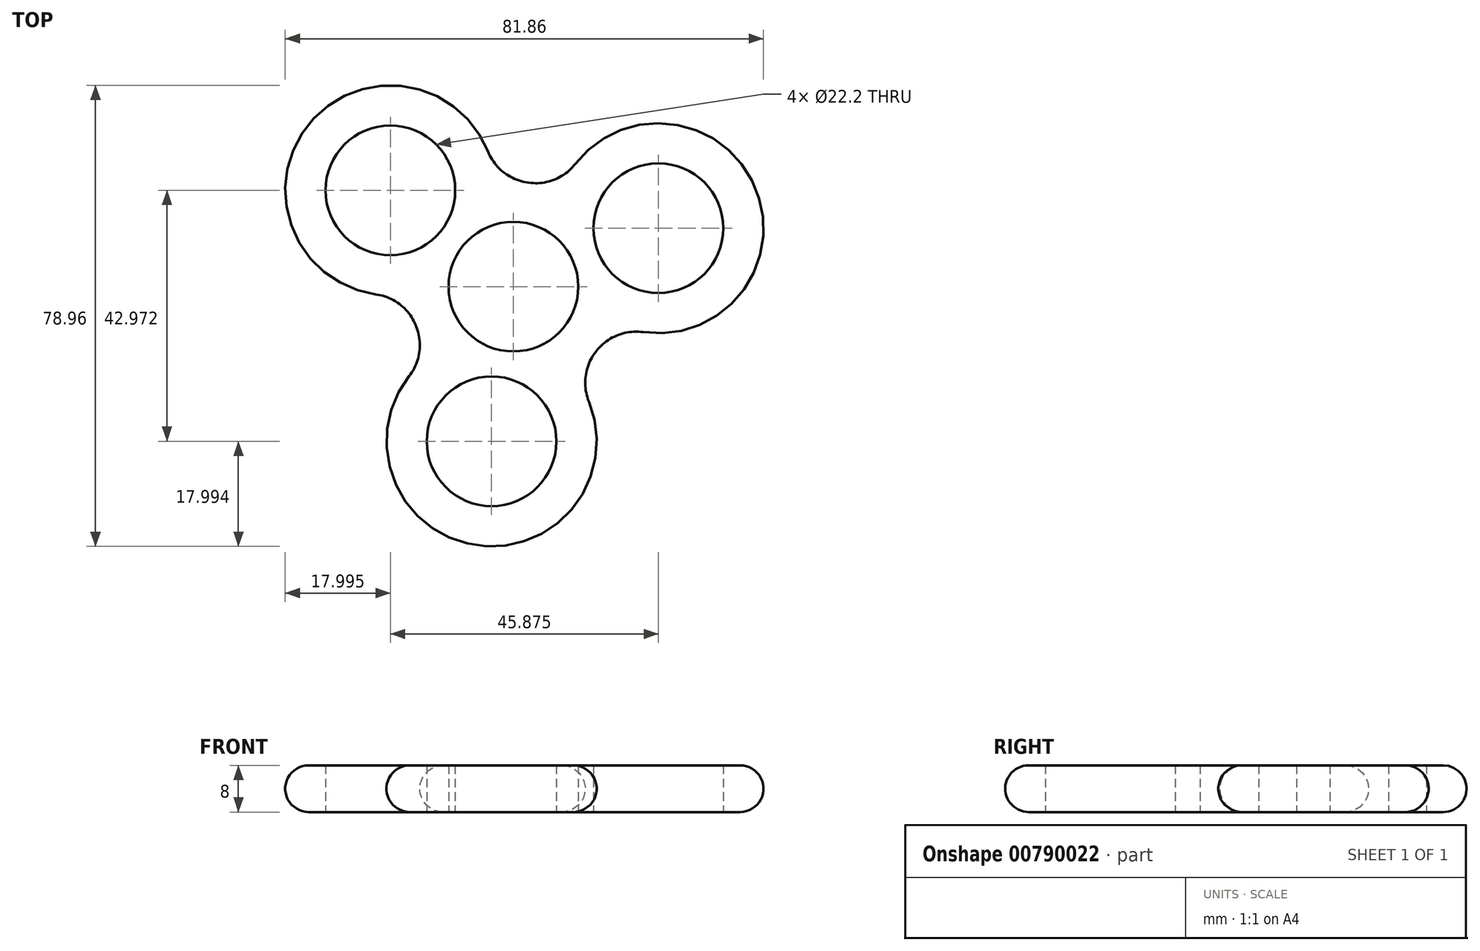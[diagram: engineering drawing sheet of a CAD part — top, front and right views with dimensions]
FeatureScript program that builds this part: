
annotation { "Feature Type Name" : "Feature", "Feature Type Description" : "" }
export const myFeature = defineFeature(function(context is Context, id is Id, definition is map)
    precondition{}
    {
        {
            var Q0;
            Q0=qCreatedBy(makeId("Top.planeOp"),FACE);
            var sketch = newSketch(context, id + "F0", { "sketchPlane" : qUnion([Q0])});
            skCircle(sketch, "E0", {"center": v(0, 0) * mm, "radius": 18 * mm});
            skCircle(sketch, "E1", {"center": v(0, 0) * mm, "radius": 11.1 * mm});
            skCircle(sketch, "E2", {"center": v(24.8, 10) * mm, "radius": 18 * mm});
            skCircle(sketch, "E3", {"center": v(24.8, 10) * mm, "radius": 11.1 * mm});
            skCircle(sketch, "E4.1.0", {"center": v(-21.07, 16.49) * mm, "radius": 18 * mm});
            skCircle(sketch, "E4.1.1", {"center": v(-21.07, 16.49) * mm, "radius": 11.1 * mm});
            skCircle(sketch, "E4.2.0", {"center": v(-3.74, -26.49) * mm, "radius": 18 * mm});
            skCircle(sketch, "E4.2.1", {"center": v(-3.74, -26.49) * mm, "radius": 11.1 * mm});
            skSolve(sketch);
        }
        {
            var Q0;
            Q0=makeQuery(id+"F0.imprint","IMPRINT",FACE,{"disambiguationData":[TD([[makeQuery(id+"F0.imprint","IMPRINT",EDGE,{"derivedFrom":sQuery(id+"F0.wireOp",EDGE,"E4.1.1")}),-1.0]])]});
            var Q1;
            {var subQ0=sQuery(id+"F0.wireOp",EDGE,"E4.1.0");var subQ1=sQuery(id+"F0.wireOp",EDGE,"E0");var subQ2=makeQuery(id+"F0.imprint","INTERSECT",VERTEX,{"disambiguationData":[OD(0.0)],"derivedFrom":[subQ1,subQ0]});Q1=makeQuery(id+"F0.imprint","IMPRINT",FACE,{"disambiguationData":[TD([[makeQuery(id+"F0.imprint","IMPRINT",EDGE,{"disambiguationData":[TD([[subQ2,-1.0]])],"derivedFrom":subQ1}),1.0]])]});}
            var Q2;
            Q2=makeQuery(id+"F0.imprint","IMPRINT",FACE,{"disambiguationData":[TD([[makeQuery(id+"F0.imprint","IMPRINT",EDGE,{"derivedFrom":sQuery(id+"F0.wireOp",EDGE,"E1")}),-1.0]])]});
            var Q3;
            {var subQ0=sQuery(id+"F0.wireOp",EDGE,"E2");var subQ1=sQuery(id+"F0.wireOp",EDGE,"E0");var subQ2=makeQuery(id+"F0.imprint","INTERSECT",VERTEX,{"disambiguationData":[OD(0.0)],"derivedFrom":[subQ1,subQ0]});Q3=makeQuery(id+"F0.imprint","IMPRINT",FACE,{"disambiguationData":[TD([[makeQuery(id+"F0.imprint","IMPRINT",EDGE,{"disambiguationData":[TD([[subQ2,1.0]])],"derivedFrom":subQ1}),1.0]])]});}
            var Q4;
            Q4=makeQuery(id+"F0.imprint","IMPRINT",FACE,{"disambiguationData":[TD([[makeQuery(id+"F0.imprint","IMPRINT",EDGE,{"derivedFrom":sQuery(id+"F0.wireOp",EDGE,"E3")}),-1.0]])]});
            var Q5;
            {var subQ0=sQuery(id+"F0.wireOp",EDGE,"E4.2.0");var subQ1=sQuery(id+"F0.wireOp",EDGE,"E0");var subQ2=makeQuery(id+"F0.imprint","INTERSECT",VERTEX,{"disambiguationData":[OD(0.0)],"derivedFrom":[subQ1,subQ0]});Q5=makeQuery(id+"F0.imprint","IMPRINT",FACE,{"disambiguationData":[TD([[makeQuery(id+"F0.imprint","IMPRINT",EDGE,{"disambiguationData":[TD([[subQ2,-1.0]])],"derivedFrom":subQ1}),1.0]])]});}
            var Q6;
            Q6=makeQuery(id+"F0.imprint","IMPRINT",FACE,{"disambiguationData":[TD([[makeQuery(id+"F0.imprint","IMPRINT",EDGE,{"derivedFrom":sQuery(id+"F0.wireOp",EDGE,"E4.2.1")}),-1.0]])]});
            extrude(context, id + "F1", {"entities" : qUnion([Q0, Q1, Q2, Q3, Q4, Q5, Q6]), "depth" : 8 * mm, "offsetDistance" : 25 * mm});
        }
        {
            var Q0;
            {var subQ0=sQuery(id+"F0.wireOp",EDGE,"E4.1.0");var subQ1=sQuery(id+"F0.wireOp",EDGE,"E0");Q0=makeQuery(id+"F1.opExtrude","SWEPT_EDGE",EDGE,{"disambiguationData":[OSD([subQ1,subQ0]),TDD([makeQuery(id+"F0.imprint","INTERSECT",VERTEX,{"disambiguationData":[OD(1.0)],"derivedFrom":[subQ1,subQ0]})])]});}
            var Q1;
            {var subQ0=sQuery(id+"F0.wireOp",EDGE,"E4.1.0");var subQ1=sQuery(id+"F0.wireOp",EDGE,"E0");Q1=makeQuery(id+"F1.opExtrude","SWEPT_EDGE",EDGE,{"disambiguationData":[OSD([subQ1,subQ0]),TDD([makeQuery(id+"F0.imprint","INTERSECT",VERTEX,{"disambiguationData":[OD(0.0)],"derivedFrom":[subQ1,subQ0]})])]});}
            var Q2;
            {var subQ0=sQuery(id+"F0.wireOp",EDGE,"E2");var subQ1=sQuery(id+"F0.wireOp",EDGE,"E0");Q2=makeQuery(id+"F1.opExtrude","SWEPT_EDGE",EDGE,{"disambiguationData":[OSD([subQ1,subQ0]),TDD([makeQuery(id+"F0.imprint","INTERSECT",VERTEX,{"disambiguationData":[OD(0.0)],"derivedFrom":[subQ1,subQ0]})])]});}
            var Q3;
            {var subQ0=sQuery(id+"F0.wireOp",EDGE,"E2");var subQ1=sQuery(id+"F0.wireOp",EDGE,"E0");Q3=makeQuery(id+"F1.opExtrude","SWEPT_EDGE",EDGE,{"disambiguationData":[OSD([subQ1,subQ0]),TDD([makeQuery(id+"F0.imprint","INTERSECT",VERTEX,{"disambiguationData":[OD(1.0)],"derivedFrom":[subQ1,subQ0]})])]});}
            var Q4;
            {var subQ0=sQuery(id+"F0.wireOp",EDGE,"E4.2.0");var subQ1=sQuery(id+"F0.wireOp",EDGE,"E0");Q4=makeQuery(id+"F1.opExtrude","SWEPT_EDGE",EDGE,{"disambiguationData":[OSD([subQ1,subQ0]),TDD([makeQuery(id+"F0.imprint","INTERSECT",VERTEX,{"disambiguationData":[OD(1.0)],"derivedFrom":[subQ1,subQ0]})])]});}
            var Q5;
            {var subQ0=sQuery(id+"F0.wireOp",EDGE,"E4.2.0");var subQ1=sQuery(id+"F0.wireOp",EDGE,"E0");Q5=makeQuery(id+"F1.opExtrude","SWEPT_EDGE",EDGE,{"disambiguationData":[OSD([subQ1,subQ0]),TDD([makeQuery(id+"F0.imprint","INTERSECT",VERTEX,{"disambiguationData":[OD(0.0)],"derivedFrom":[subQ1,subQ0]})])]});}
            fillet(context, id + "F2", {"entities" : qUnion([Q0, Q1, Q2, Q3, Q4, Q5]), "radius" : 8.55 * mm, "tangentPropagation" : true, "allowEdgeOverflow" : false});
        }
        {
            var Q0;
            {var subQ0=sQuery(id+"F0.wireOp",EDGE,"E4.2.0");var subQ1=sQuery(id+"F0.wireOp",EDGE,"E0");Q0=makeQuery(id+"F2.opFillet","BLEND_EDGE",EDGE,{"blendedFrom":[makeQuery(id+"F1.opExtrude","SWEPT_EDGE",EDGE,{"disambiguationData":[OSD([subQ1,subQ0]),TDD([makeQuery(id+"F0.imprint","INTERSECT",VERTEX,{"disambiguationData":[OD(1.0)],"derivedFrom":[subQ1,subQ0]})])]}),makeQuery(id+"F1.opExtrude","CAP_FACE",FACE,{"disambiguationData":[OSD([subQ1,sQuery(id+"F0.wireOp",EDGE,"E1"),sQuery(id+"F0.wireOp",EDGE,"E2"),sQuery(id+"F0.wireOp",EDGE,"E3"),sQuery(id+"F0.wireOp",EDGE,"E4.1.0"),sQuery(id+"F0.wireOp",EDGE,"E4.1.1"),subQ0,sQuery(id+"F0.wireOp",EDGE,"E4.2.1")])],"isStart":false})],"blendedInto":[makeQuery(id+"F1.opExtrude","CAP_FACE",FACE,{"disambiguationData":[OSD([subQ1,sQuery(id+"F0.wireOp",EDGE,"E1"),sQuery(id+"F0.wireOp",EDGE,"E2"),sQuery(id+"F0.wireOp",EDGE,"E3"),sQuery(id+"F0.wireOp",EDGE,"E4.1.0"),sQuery(id+"F0.wireOp",EDGE,"E4.1.1"),subQ0,sQuery(id+"F0.wireOp",EDGE,"E4.2.1")])],"isStart":false})]});}
            var Q1;
            Q1=makeQuery(id+"F1.opExtrude","CAP_EDGE",EDGE,{"disambiguationData":[OSD([sQuery(id+"F0.wireOp",EDGE,"E4.2.0")])],"isStart":true});
            fillet(context, id + "F3", {"entities" : qUnion([Q0, Q1]), "radius" : 4 * mm, "tangentPropagation" : true, "allowEdgeOverflow" : false});
        }
    });
